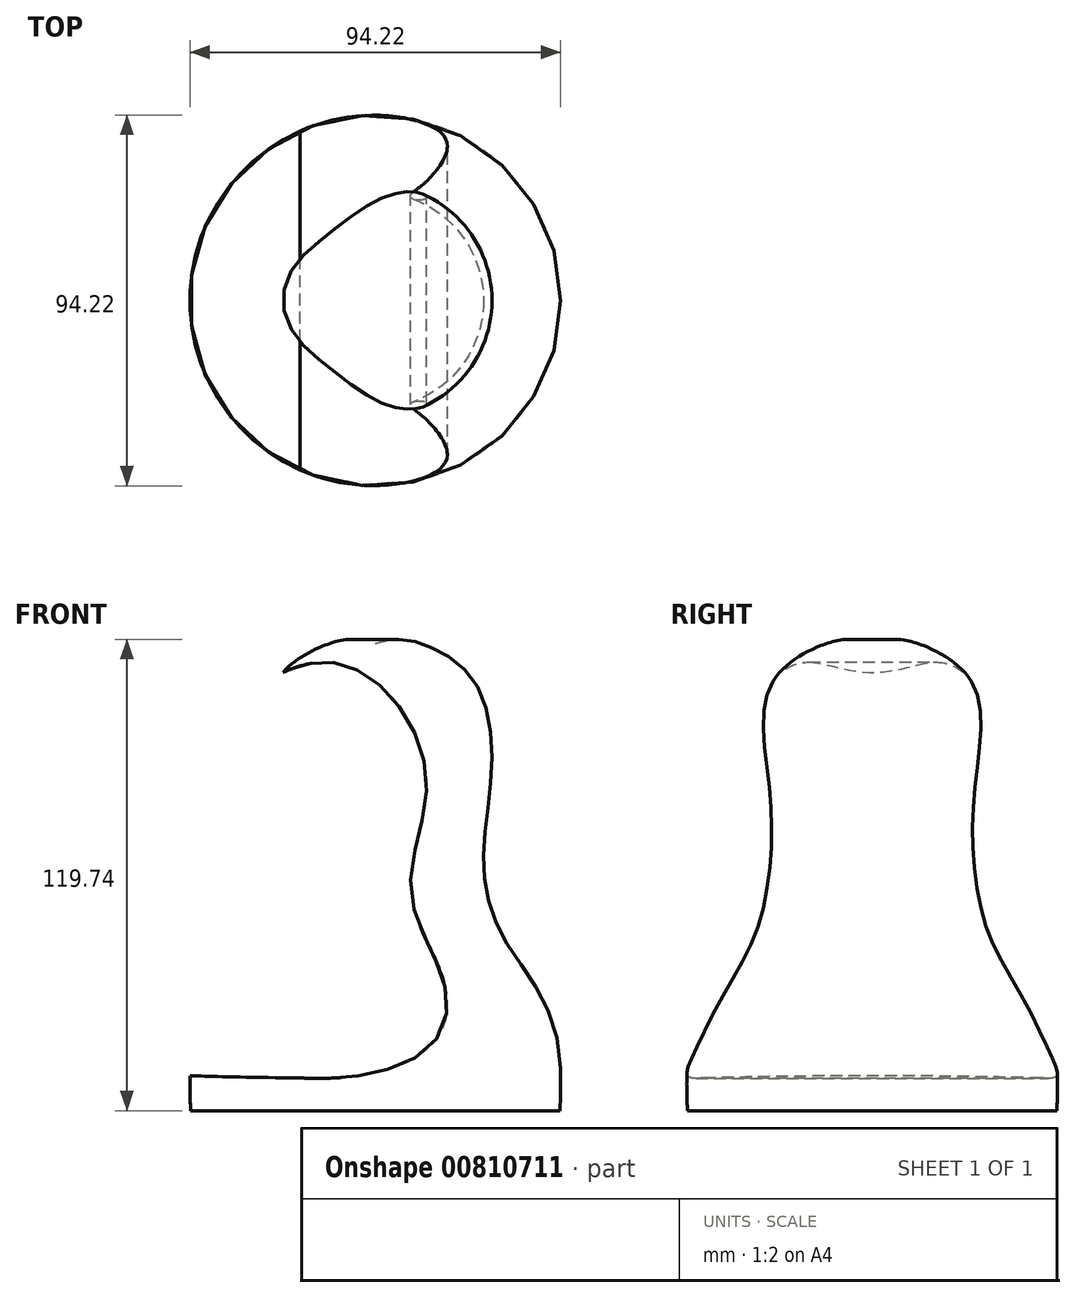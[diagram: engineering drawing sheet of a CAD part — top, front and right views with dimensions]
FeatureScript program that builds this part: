
annotation { "Feature Type Name" : "Feature", "Feature Type Description" : "" }
export const myFeature = defineFeature(function(context is Context, id is Id, definition is map)
    precondition{}
    {
        {
            var Q0;
            Q0=qCreatedBy(makeId("Front.planeOp"),FACE);
            var sketch = newSketch(context, id + "F0", { "sketchPlane" : qUnion([Q0])});
            skFitSpline(sketch, "E0", {"points": [v(0, 64.12) * mm, v(12.14, 63.91) * mm, v(24.87, 55) * mm, v(29.57, 32.79) * mm, v(27.5, 9.34) * mm, v(32.68, -10.8) * mm, v(45.96, -35.28) * mm, v(47, -55) * mm, v(47.2, -54.58) * mm], "startDerivative": vector(149.67, 45.18) * mm, "endDerivative": vector(11.27, 30.97) * mm});
            skLineSegment(sketch, "E1", {"start": v(47.2, -54.58) * mm, "end": v(0, -54.58) * mm});
            skLineSegment(sketch, "E2", {"start": v(0, 64.12) * mm, "end": v(0, -54.58) * mm});
            skSolve(sketch);
        }
        {
            var Q0;
            {var subQ0=sQuery(id+"F0.wireOp",EDGE,"E2");Q0=makeQuery(id+"F0.imprint","IMPRINT",FACE,{"disambiguationData":[TD([[makeQuery(id+"F0.imprint","IMPRINT",EDGE,{"derivedFrom":subQ0}),1.0]])]});}
            var Q1;
            Q1=sQuery(id+"F0.wireOp",EDGE,"E2");
            revolve(context, id + "F1", {"surfaceOperationType" : NewSurfaceOperationType.NEW, "entities" : qUnion([Q0]), "axis" : qUnion([Q1]), "revolveType" : RevolveType.FULL});
        }
        {
            var Q0;
            Q0=qCreatedBy(makeId("Front.planeOp"),FACE);
            var sketch = newSketch(context, id + "F2", { "sketchPlane" : qUnion([Q0])});
            skFitSpline(sketch, "E3", {"points": [v(-58.5, 16.14) * mm, v(-11.54, 59.32) * mm, v(12.84, 31.33) * mm, v(8.98, 1.24) * mm, v(18.04, -24.56) * mm, v(7.99, -42.3) * mm, v(-52.6, -35.59) * mm, v(-58.5, 16.14) * mm]});
            skFitSpline(sketch, "E4", {"points": [v(-19.12, -46.26) * mm, v(-53.28, -45.44) * mm, v(-65.22, -43.2) * mm, v(-52.6, -35.59) * mm], "startDerivative": vector(-80.51, 0.9) * mm, "endDerivative": vector(65.94, 30.6) * mm});
            skSolve(sketch);
        }
        {
            var Q0;
            Q0=qSketchRegion(id+"F2",true);
            extrude(context, id + "F3", {"entities" : qUnion([Q0]), "operationType" : NewBodyOperationType.REMOVE, "depth" : 103.8 * mm, "offsetDistance" : 25 * mm, "symmetric" : true});
        }
    });
